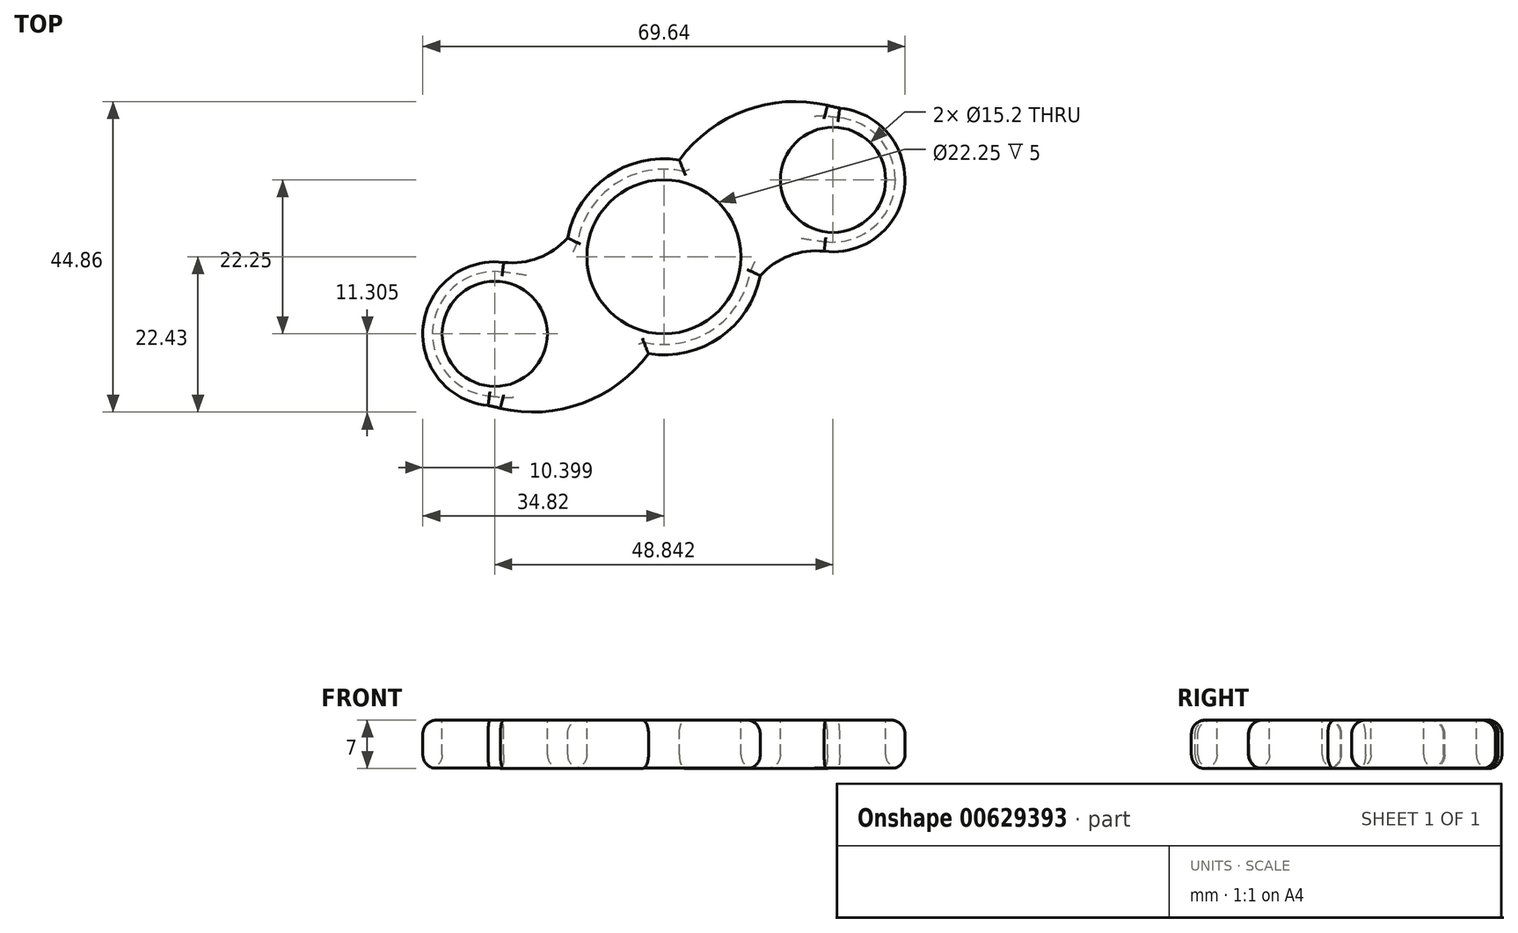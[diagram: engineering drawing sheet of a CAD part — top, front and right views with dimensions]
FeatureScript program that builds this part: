
annotation { "Feature Type Name" : "Feature", "Feature Type Description" : "" }
export const myFeature = defineFeature(function(context is Context, id is Id, definition is map)
    precondition{}
    {
        {
            var Q0;
            Q0=qCreatedBy(makeId("Top.planeOp"),FACE);
            var sketch = newSketch(context, id + "F0", { "sketchPlane" : qUnion([Q0])});
            skCircle(sketch, "E0", {"center": v(0, 0) * mm, "radius": 11.12 * mm});
            skCircle(sketch, "E1", {"center": v(0, 0) * mm, "radius": 14.18 * mm});
            skLineSegment(sketch, "E2", {"start": v(0, 0) * mm, "end": v(35.77, 0) * mm, "construction": true});
            skLineSegment(sketch, "E3", {"start": v(0, 11.12) * mm, "end": v(34.82, 11.12) * mm, "construction": true});
            skCircle(sketch, "E4", {"center": v(24.42, 11.12) * mm, "radius": 7.6 * mm});
            skCircle(sketch, "E5", {"center": v(24.42, 11.12) * mm, "radius": 10.4 * mm});
            skArc(sketch, "E6", {"start": v(23.3, 0.79) * mm, "mid": v(18.17, 0.18) * mm, "end": v(13.91, -2.73) * mm});
            skArc(sketch, "E7", {"start": v(23.63, 21.89) * mm, "mid": v(11.74, 21.15) * mm, "end": v(2.22, 14) * mm});
            skArc(sketch, "E8", {"start": v(23.63, 21.89) * mm, "mid": v(25.04, 21.54) * mm, "end": v(26.48, 21.32) * mm});
            skPoint(sketch, "E8.first.point", {"position": v(23.63, 21.89) * mm});
            skPoint(sketch, "E8.second.point", {"position": v(26.48, 21.32) * mm});
            skPoint(sketch, "E8.third.point", {"position": v(19.65, 23.55) * mm});
            skPoint(sketch, "E9.1.0", {"position": v(-19.65, -23.55) * mm});
            skLineSegment(sketch, "E9.1.1", {"start": v(0, -11.12) * mm, "end": v(-34.82, -11.12) * mm, "construction": true});
            skPoint(sketch, "E9.1.2", {"position": v(-26.48, -21.32) * mm});
            skCircle(sketch, "E9.1.3", {"center": v(-24.42, -11.12) * mm, "radius": 7.6 * mm});
            skLineSegment(sketch, "E9.1.4", {"start": v(0, 0) * mm, "end": v(-35.77, 0) * mm, "construction": true});
            skCircle(sketch, "E9.1.5", {"center": v(-24.42, -11.12) * mm, "radius": 10.4 * mm});
            skArc(sketch, "E9.1.6", {"start": v(-23.3, -0.79) * mm, "mid": v(-18.17, -0.18) * mm, "end": v(-13.91, 2.73) * mm});
            skArc(sketch, "E9.1.7", {"start": v(-23.63, -21.89) * mm, "mid": v(-11.74, -21.15) * mm, "end": v(-2.22, -14) * mm});
            skPoint(sketch, "E9.1.8", {"position": v(-23.63, -21.89) * mm});
            skArc(sketch, "E9.1.9", {"start": v(-23.63, -21.89) * mm, "mid": v(-25.04, -21.54) * mm, "end": v(-26.48, -21.32) * mm});
            skSolve(sketch);
        }
        {
            var Q0;
            {var subQ5=sQuery(id+"F0.wireOp",EDGE,"E9.1.7");Q0=makeQuery(id+"F0.imprint","IMPRINT",FACE,{"disambiguationData":[TD([[makeQuery(id+"F0.imprint","IMPRINT",EDGE,{"derivedFrom":subQ5}),1.0]])]});}
            var Q1;
            {var subQ5=sQuery(id+"F0.wireOp",EDGE,"E7");Q1=makeQuery(id+"F0.imprint","IMPRINT",FACE,{"disambiguationData":[TD([[makeQuery(id+"F0.imprint","IMPRINT",EDGE,{"derivedFrom":subQ5}),1.0]])]});}
            var Q2;
            Q2=makeQuery(id+"F0.imprint","IMPRINT",FACE,{"disambiguationData":[TD([[makeQuery(id+"F0.imprint","IMPRINT",EDGE,{"derivedFrom":sQuery(id+"F0.wireOp",EDGE,"E0")}),-1.0]])]});
            var Q3;
            Q3=makeQuery(id+"F0.imprint","IMPRINT",FACE,{"disambiguationData":[TD([[makeQuery(id+"F0.imprint","IMPRINT",EDGE,{"derivedFrom":sQuery(id+"F0.wireOp",EDGE,"E4")}),-1.0]])]});
            var Q4;
            Q4=makeQuery(id+"F0.imprint","IMPRINT",FACE,{"disambiguationData":[TD([[makeQuery(id+"F0.imprint","IMPRINT",EDGE,{"derivedFrom":sQuery(id+"F0.wireOp",EDGE,"E9.1.3")}),-1.0]])]});
            var Q5;
            {var subQ0=sQuery(id+"F0.wireOp",EDGE,"E6");var subQ1=sQuery(id+"F0.wireOp",EDGE,"E5");var subQ2=makeQuery(id+"F0.imprint","INTERSECT",VERTEX,{"disambiguationData":[OD(0.0)],"derivedFrom":[subQ1,subQ0]});Q5=makeQuery(id+"F0.imprint","IMPRINT",FACE,{"disambiguationData":[TD([[makeQuery(id+"F0.imprint","IMPRINT",EDGE,{"disambiguationData":[TD([[subQ2,1.0]])],"derivedFrom":subQ1}),1.0]])]});}
            var Q6;
            {var subQ0=sQuery(id+"F0.wireOp",EDGE,"E9.1.6");var subQ1=sQuery(id+"F0.wireOp",EDGE,"E9.1.5");var subQ2=makeQuery(id+"F0.imprint","INTERSECT",VERTEX,{"disambiguationData":[OD(0.0)],"derivedFrom":[subQ1,subQ0]});Q6=makeQuery(id+"F0.imprint","IMPRINT",FACE,{"disambiguationData":[TD([[makeQuery(id+"F0.imprint","IMPRINT",EDGE,{"disambiguationData":[TD([[subQ2,1.0]])],"derivedFrom":subQ1}),1.0]])]});}
            var Q7;
            {var subQ0=sQuery(id+"F0.wireOp",EDGE,"E8");var subQ1=sQuery(id+"F0.wireOp",EDGE,"E5");var subQ2=makeQuery(id+"F0.imprint","INTERSECT",VERTEX,{"disambiguationData":[OD(0.0)],"derivedFrom":[subQ1,subQ0]});Q7=makeQuery(id+"F0.imprint","IMPRINT",FACE,{"disambiguationData":[TD([[makeQuery(id+"F0.imprint","IMPRINT",EDGE,{"disambiguationData":[TD([[subQ2,-1.0]])],"derivedFrom":subQ1}),1.0]])]});}
            var Q8;
            {var subQ0=sQuery(id+"F0.wireOp",EDGE,"E9.1.9");var subQ1=sQuery(id+"F0.wireOp",EDGE,"E9.1.5");var subQ2=makeQuery(id+"F0.imprint","INTERSECT",VERTEX,{"disambiguationData":[OD(0.0)],"derivedFrom":[subQ1,subQ0]});Q8=makeQuery(id+"F0.imprint","IMPRINT",FACE,{"disambiguationData":[TD([[makeQuery(id+"F0.imprint","IMPRINT",EDGE,{"disambiguationData":[TD([[subQ2,-1.0]])],"derivedFrom":subQ1}),1.0]])]});}
            extrude(context, id + "F1", {"entities" : qUnion([Q0, Q1, Q2, Q3, Q4, Q5, Q6, Q7, Q8]), "oppositeDirection" : true, "depth" : 7 * mm, "offsetDistance" : 25 * mm});
        }
        {
            var Q0;
            Q0=makeQuery(id+"F1.opExtrude","CAP_EDGE",EDGE,{"disambiguationData":[OSD([sQuery(id+"F0.wireOp",EDGE,"E9.1.5")])],"isStart":true});
            var Q1;
            Q1=makeQuery(id+"F1.opExtrude","CAP_EDGE",EDGE,{"disambiguationData":[OSD([sQuery(id+"F0.wireOp",EDGE,"E9.1.7")])],"isStart":true});
            var Q2;
            {var subQ0=sQuery(id+"F0.wireOp",EDGE,"E1");Q2=makeQuery(id+"F1.opExtrude","CAP_EDGE",EDGE,{"disambiguationData":[OSD([subQ0]),TDD([makeQuery(id+"F0.imprint","IMPRINT",EDGE,{"disambiguationData":[TD([[makeQuery(id+"F0.imprint","INTERSECT",VERTEX,{"derivedFrom":[subQ0,sQuery(id+"F0.wireOp",EDGE,"E7")]}),-1.0]])],"derivedFrom":subQ0})])],"isStart":true});}
            var Q3;
            Q3=makeQuery(id+"F1.opExtrude","CAP_EDGE",EDGE,{"disambiguationData":[OSD([sQuery(id+"F0.wireOp",EDGE,"E6")])],"isStart":true});
            var Q4;
            {var subQ0=sQuery(id+"F0.wireOp",EDGE,"E1");Q4=makeQuery(id+"F1.opExtrude","CAP_EDGE",EDGE,{"disambiguationData":[OSD([subQ0]),TDD([makeQuery(id+"F0.imprint","IMPRINT",EDGE,{"disambiguationData":[TD([[makeQuery(id+"F0.imprint","INTERSECT",VERTEX,{"derivedFrom":[subQ0,sQuery(id+"F0.wireOp",EDGE,"E6")]}),1.0]])],"derivedFrom":subQ0})])],"isStart":true});}
            var Q5;
            Q5=makeQuery(id+"F1.opExtrude","CAP_EDGE",EDGE,{"disambiguationData":[OSD([sQuery(id+"F0.wireOp",EDGE,"E5")])],"isStart":true});
            var Q6;
            Q6=makeQuery(id+"F1.opExtrude","CAP_EDGE",EDGE,{"disambiguationData":[OSD([sQuery(id+"F0.wireOp",EDGE,"E7")])],"isStart":true});
            var Q7;
            Q7=makeQuery(id+"F1.opExtrude","CAP_EDGE",EDGE,{"disambiguationData":[OSD([sQuery(id+"F0.wireOp",EDGE,"E5")])],"isStart":false});
            var Q8;
            Q8=makeQuery(id+"F1.opExtrude","CAP_EDGE",EDGE,{"disambiguationData":[OSD([sQuery(id+"F0.wireOp",EDGE,"E7")])],"isStart":false});
            var Q9;
            Q9=makeQuery(id+"F1.opExtrude","CAP_EDGE",EDGE,{"disambiguationData":[OSD([sQuery(id+"F0.wireOp",EDGE,"E8")])],"isStart":false});
            var Q10;
            Q10=makeQuery(id+"F1.opExtrude","CAP_FACE",FACE,{"disambiguationData":[OSD([sQuery(id+"F0.wireOp",EDGE,"E0"),sQuery(id+"F0.wireOp",EDGE,"E1"),sQuery(id+"F0.wireOp",EDGE,"E4"),sQuery(id+"F0.wireOp",EDGE,"E5"),sQuery(id+"F0.wireOp",EDGE,"E6"),sQuery(id+"F0.wireOp",EDGE,"E7"),sQuery(id+"F0.wireOp",EDGE,"E8"),sQuery(id+"F0.wireOp",EDGE,"E9.1.3"),sQuery(id+"F0.wireOp",EDGE,"E9.1.5"),sQuery(id+"F0.wireOp",EDGE,"E9.1.6"),sQuery(id+"F0.wireOp",EDGE,"E9.1.7"),sQuery(id+"F0.wireOp",EDGE,"E9.1.9")])],"isStart":false});
            fillet(context, id + "F2", {"entities" : qUnion([Q0, Q1, Q2, Q3, Q4, Q5, Q6, Q7, Q8, Q9, Q10]), "radius" : 2 * mm, "tangentPropagation" : true, "allowEdgeOverflow" : false});
        }
    });
